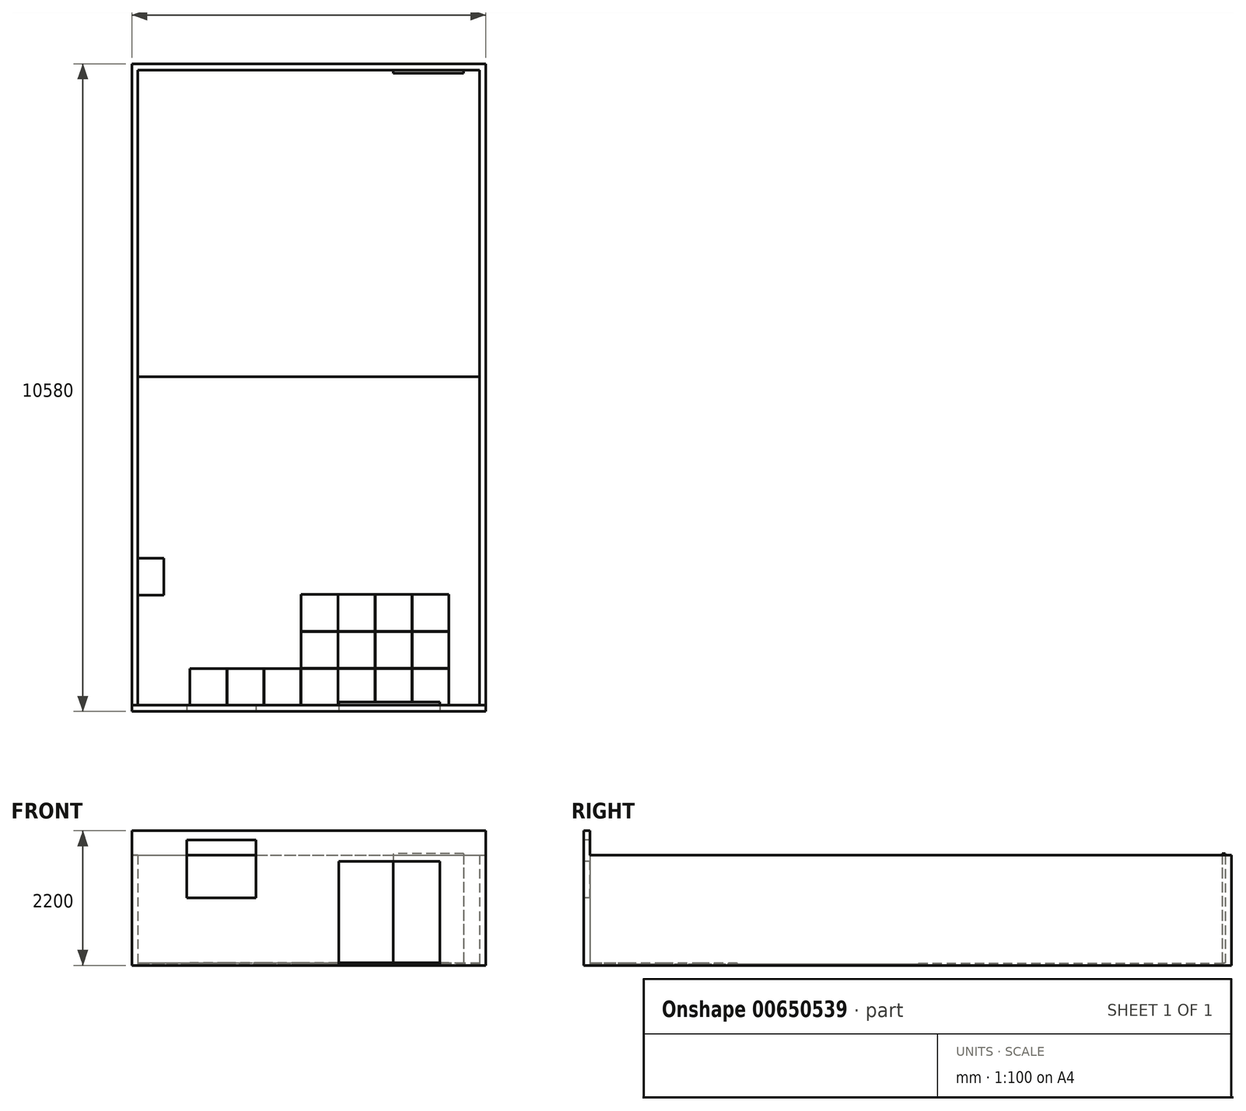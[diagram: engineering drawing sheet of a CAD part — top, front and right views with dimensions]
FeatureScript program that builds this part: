
annotation { "Feature Type Name" : "Feature", "Feature Type Description" : "" }
export const myFeature = defineFeature(function(context is Context, id is Id, definition is map)
    precondition{}
    {
        {
            var Q0;
            Q0=qCreatedBy(makeId("Top.planeOp"),FACE);
            var sketch = newSketch(context, id + "F0", { "sketchPlane" : qUnion([Q0])});
            skLineSegment(sketch, "E0.bottom", {"start": v(0, 0) * mm, "end": v(-5580, 0) * mm});
            skLineSegment(sketch, "E0.top", {"start": v(0, 10380) * mm, "end": v(-5580, 10380) * mm});
            skLineSegment(sketch, "E0.left", {"start": v(0, 0) * mm, "end": v(0, 10380) * mm});
            skLineSegment(sketch, "E0.right", {"start": v(-5580, 0) * mm, "end": v(-5580, 10380) * mm});
            skSolve(sketch);
        }
        {
            var Q0;
            Q0 = qSketchRegion(id + "F0", true);
            extrude(context, id + "F1", {"entities" : qUnion([Q0]), "depth" : 25 * mm, "offsetDistance" : 25 * mm});
        }
        {
            var Q0;
            Q0=makeQuery(id+"F1.opExtrude","CAP_FACE",FACE,{"disambiguationData":[OSD([sQuery(id+"F0.wireOp",EDGE,"E0.bottom"),sQuery(id+"F0.wireOp",EDGE,"E0.top"),sQuery(id+"F0.wireOp",EDGE,"E0.left"),sQuery(id+"F0.wireOp",EDGE,"E0.right")])],"isStart":false});
            var sketch = newSketch(context, id + "F2", { "sketchPlane" : qUnion([Q0])});
            skLineSegment(sketch, "E1.bottom", {"start": v(-500, 0) * mm, "end": v(-1100, 0) * mm});
            skLineSegment(sketch, "E1.top", {"start": v(-500, 600) * mm, "end": v(-1100, 600) * mm});
            skLineSegment(sketch, "E1.left", {"start": v(-500, 0) * mm, "end": v(-500, 600) * mm});
            skLineSegment(sketch, "E1.right", {"start": v(-1100, 0) * mm, "end": v(-1100, 600) * mm});
            skLineSegment(sketch, "E2.0.1.0", {"start": v(-500, 605) * mm, "end": v(-1100, 605) * mm});
            skLineSegment(sketch, "E2.0.1.1", {"start": v(-500, 1205) * mm, "end": v(-1100, 1205) * mm});
            skLineSegment(sketch, "E2.0.1.2", {"start": v(-500, 605) * mm, "end": v(-500, 1205) * mm});
            skLineSegment(sketch, "E2.0.1.3", {"start": v(-1100, 605) * mm, "end": v(-1100, 1205) * mm});
            skLineSegment(sketch, "E2.1.0.0", {"start": v(-1105, 0) * mm, "end": v(-1705, 0) * mm});
            skLineSegment(sketch, "E2.1.0.1", {"start": v(-1105, 600) * mm, "end": v(-1705, 600) * mm});
            skLineSegment(sketch, "E2.1.0.2", {"start": v(-1105, 0) * mm, "end": v(-1105, 600) * mm});
            skLineSegment(sketch, "E2.1.0.3", {"start": v(-1705, 0) * mm, "end": v(-1705, 600) * mm});
            skLineSegment(sketch, "E2.1.1.0", {"start": v(-1105, 605) * mm, "end": v(-1705, 605) * mm});
            skLineSegment(sketch, "E2.1.1.1", {"start": v(-1105, 1205) * mm, "end": v(-1705, 1205) * mm});
            skLineSegment(sketch, "E2.1.1.2", {"start": v(-1105, 605) * mm, "end": v(-1105, 1205) * mm});
            skLineSegment(sketch, "E2.1.1.3", {"start": v(-1705, 605) * mm, "end": v(-1705, 1205) * mm});
            skLineSegment(sketch, "E2.2.0.0", {"start": v(-1710, 0) * mm, "end": v(-2310, 0) * mm});
            skLineSegment(sketch, "E2.2.0.1", {"start": v(-1710, 600) * mm, "end": v(-2310, 600) * mm});
            skLineSegment(sketch, "E2.2.0.2", {"start": v(-1710, 0) * mm, "end": v(-1710, 600) * mm});
            skLineSegment(sketch, "E2.2.0.3", {"start": v(-2310, 0) * mm, "end": v(-2310, 600) * mm});
            skLineSegment(sketch, "E2.2.1.0", {"start": v(-1710, 605) * mm, "end": v(-2310, 605) * mm});
            skLineSegment(sketch, "E2.2.1.1", {"start": v(-1710, 1205) * mm, "end": v(-2310, 1205) * mm});
            skLineSegment(sketch, "E2.2.1.2", {"start": v(-1710, 605) * mm, "end": v(-1710, 1205) * mm});
            skLineSegment(sketch, "E2.2.1.3", {"start": v(-2310, 605) * mm, "end": v(-2310, 1205) * mm});
            skLineSegment(sketch, "E2.3.0.0", {"start": v(-2315, 0) * mm, "end": v(-2915, 0) * mm});
            skLineSegment(sketch, "E2.3.0.1", {"start": v(-2315, 600) * mm, "end": v(-2915, 600) * mm});
            skLineSegment(sketch, "E2.3.0.2", {"start": v(-2315, 0) * mm, "end": v(-2315, 600) * mm});
            skLineSegment(sketch, "E2.3.0.3", {"start": v(-2915, 0) * mm, "end": v(-2915, 600) * mm});
            skLineSegment(sketch, "E2.3.1.0", {"start": v(-2315, 605) * mm, "end": v(-2915, 605) * mm});
            skLineSegment(sketch, "E2.3.1.1", {"start": v(-2315, 1205) * mm, "end": v(-2915, 1205) * mm});
            skLineSegment(sketch, "E2.3.1.2", {"start": v(-2315, 605) * mm, "end": v(-2315, 1205) * mm});
            skLineSegment(sketch, "E2.3.1.3", {"start": v(-2915, 605) * mm, "end": v(-2915, 1205) * mm});
            skLineSegment(sketch, "E2.direction1", {"start": v(-1100, 0) * mm, "end": v(-1705, 0) * mm, "construction": true});
            skLineSegment(sketch, "E2.direction2", {"start": v(-1100, 0) * mm, "end": v(-1100, 605) * mm, "construction": true});
            skLineSegment(sketch, "E3.0.0.2", {"start": v(-500, 1210) * mm, "end": v(-1100, 1210) * mm});
            skLineSegment(sketch, "E3.3.0.2", {"start": v(-500, 1810) * mm, "end": v(-1100, 1810) * mm});
            skLineSegment(sketch, "E3.6.0.2", {"start": v(-500, 1210) * mm, "end": v(-500, 1810) * mm});
            skLineSegment(sketch, "E3.9.0.2", {"start": v(-1100, 1210) * mm, "end": v(-1100, 1810) * mm});
            skLineSegment(sketch, "E3.0.1.2", {"start": v(-1105, 1210) * mm, "end": v(-1705, 1210) * mm});
            skLineSegment(sketch, "E3.3.1.2", {"start": v(-1105, 1810) * mm, "end": v(-1705, 1810) * mm});
            skLineSegment(sketch, "E3.6.1.2", {"start": v(-1105, 1210) * mm, "end": v(-1105, 1810) * mm});
            skLineSegment(sketch, "E3.9.1.2", {"start": v(-1705, 1210) * mm, "end": v(-1705, 1810) * mm});
            skLineSegment(sketch, "E3.0.2.2", {"start": v(-1710, 1210) * mm, "end": v(-2310, 1210) * mm});
            skLineSegment(sketch, "E3.3.2.2", {"start": v(-1710, 1810) * mm, "end": v(-2310, 1810) * mm});
            skLineSegment(sketch, "E3.6.2.2", {"start": v(-1710, 1210) * mm, "end": v(-1710, 1810) * mm});
            skLineSegment(sketch, "E3.9.2.2", {"start": v(-2310, 1210) * mm, "end": v(-2310, 1810) * mm});
            skLineSegment(sketch, "E3.0.3.2", {"start": v(-2315, 1210) * mm, "end": v(-2915, 1210) * mm});
            skLineSegment(sketch, "E3.3.3.2", {"start": v(-2315, 1810) * mm, "end": v(-2915, 1810) * mm});
            skLineSegment(sketch, "E3.6.3.2", {"start": v(-2315, 1210) * mm, "end": v(-2315, 1810) * mm});
            skLineSegment(sketch, "E3.9.3.2", {"start": v(-2915, 1210) * mm, "end": v(-2915, 1810) * mm});
            skLineSegment(sketch, "E4.bottom", {"start": v(-500, 1815) * mm, "end": v(-1100, 1815) * mm});
            skLineSegment(sketch, "E5.direction1", {"start": v(-1100, 1810) * mm, "end": v(-1075, 1810) * mm, "construction": true});
            skLineSegment(sketch, "E6.bottom", {"start": v(-2920, 0) * mm, "end": v(-3520, 0) * mm});
            skLineSegment(sketch, "E6.top", {"start": v(-2920, 600) * mm, "end": v(-3520, 600) * mm});
            skLineSegment(sketch, "E6.left", {"start": v(-2920, 0) * mm, "end": v(-2920, 600) * mm});
            skLineSegment(sketch, "E6.right", {"start": v(-3520, 0) * mm, "end": v(-3520, 600) * mm});
            skLineSegment(sketch, "E7.1.0.0", {"start": v(-3525, 0) * mm, "end": v(-4125, 0) * mm});
            skLineSegment(sketch, "E7.1.0.1", {"start": v(-3525, 0) * mm, "end": v(-3525, 600) * mm});
            skLineSegment(sketch, "E7.1.0.2", {"start": v(-3525, 600) * mm, "end": v(-4125, 600) * mm});
            skLineSegment(sketch, "E7.1.0.3", {"start": v(-4125, 0) * mm, "end": v(-4125, 600) * mm});
            skLineSegment(sketch, "E7.2.0.0", {"start": v(-4130, 0) * mm, "end": v(-4730, 0) * mm});
            skLineSegment(sketch, "E7.2.0.1", {"start": v(-4130, 0) * mm, "end": v(-4130, 600) * mm});
            skLineSegment(sketch, "E7.2.0.2", {"start": v(-4130, 600) * mm, "end": v(-4730, 600) * mm});
            skLineSegment(sketch, "E7.2.0.3", {"start": v(-4730, 0) * mm, "end": v(-4730, 600) * mm});
            skLineSegment(sketch, "E7.2.0.4", {"start": v(-4125, 0) * mm, "end": v(-4125, 600) * mm});
            skLineSegment(sketch, "E7.direction1", {"start": v(-3520, 0) * mm, "end": v(-4125, 0) * mm, "construction": true});
            skSolve(sketch);
        }
        {
            var Q0;
            Q0 = qSketchRegion(id + "F2", true);
            var Q1;
            Q1=makeQuery(id+"F2.imprint","IMPRINT",FACE,{"disambiguationData":[TD([[makeQuery(id+"F2.imprint","IMPRINT",EDGE,{"derivedFrom":sQuery(id+"F2.wireOp",EDGE,"E2.2.1.0")}),-1.0]])]});
            var Q2;
            Q2=makeQuery(id+"F2.imprint","IMPRINT",FACE,{"disambiguationData":[TD([[makeQuery(id+"F2.imprint","IMPRINT",EDGE,{"derivedFrom":sQuery(id+"F2.wireOp",EDGE,"E2.1.1.0")}),-1.0]])]});
            extrude(context, id + "F3", {"entities" : qUnion([Q0, Q1, Q2]), "depth" : 15 * mm, "offsetDistance" : 25 * mm});
        }
        {
            var Q0;
            Q0=qCreatedBy(makeId("Top.planeOp"),FACE);
            var sketch = newSketch(context, id + "F4", { "sketchPlane" : qUnion([Q0])});
            skLineSegment(sketch, "E8.bottom", {"start": v(0, 0) * mm, "end": v(100, 0) * mm});
            skLineSegment(sketch, "E8.top", {"start": v(0, 10380) * mm, "end": v(100, 10380) * mm});
            skLineSegment(sketch, "E8.left", {"start": v(0, 0) * mm, "end": v(0, 10380) * mm});
            skLineSegment(sketch, "E8.right", {"start": v(100, 0) * mm, "end": v(100, 10380) * mm});
            skSolve(sketch);
        }
        {
            var Q0;
            Q0 = qSketchRegion(id + "F4", true);
            extrude(context, id + "F5", {"entities" : qUnion([Q0]), "operationType" : NewBodyOperationType.ADD, "depth" : 1800 * mm, "offsetDistance" : 25 * mm});
        }
        {
            var Q0;
            Q0=qCreatedBy(makeId("Top.planeOp"),FACE);
            var sketch = newSketch(context, id + "F6", { "sketchPlane" : qUnion([Q0])});
            skLineSegment(sketch, "E9.bottom", {"start": v(-5580, 10380) * mm, "end": v(100, 10380) * mm});
            skLineSegment(sketch, "E9.top", {"start": v(-5580, 10480) * mm, "end": v(100, 10480) * mm});
            skLineSegment(sketch, "E9.left", {"start": v(-5580, 10380) * mm, "end": v(-5580, 10480) * mm});
            skLineSegment(sketch, "E9.right", {"start": v(100, 10380) * mm, "end": v(100, 10480) * mm});
            skSolve(sketch);
        }
        {
            var Q0;
            Q0=makeQuery(id+"F6.imprint","IMPRINT",FACE,{"disambiguationData":[TD([[makeQuery(id+"F6.imprint","IMPRINT",EDGE,{"derivedFrom":sQuery(id+"F6.wireOp",EDGE,"E9.top")}),-1.0]])]});
            extrude(context, id + "F7", {"entities" : qUnion([Q0]), "operationType" : NewBodyOperationType.ADD, "depth" : 1800 * mm, "offsetDistance" : 25 * mm});
        }
        {
            var Q0;
            Q0=qCreatedBy(makeId("Top.planeOp"),FACE);
            var sketch = newSketch(context, id + "F8", { "sketchPlane" : qUnion([Q0])});
            skLineSegment(sketch, "E10.bottom", {"start": v(-5580, 0) * mm, "end": v(-5680, 0) * mm});
            skLineSegment(sketch, "E10.top", {"start": v(-5580, 10480) * mm, "end": v(-5680, 10480) * mm});
            skLineSegment(sketch, "E10.left", {"start": v(-5580, 0) * mm, "end": v(-5580, 10480) * mm});
            skLineSegment(sketch, "E10.right", {"start": v(-5680, 0) * mm, "end": v(-5680, 10480) * mm});
            skSolve(sketch);
        }
        {
            var Q0;
            Q0 = qSketchRegion(id + "F8", true);
            extrude(context, id + "F9", {"entities" : qUnion([Q0]), "operationType" : NewBodyOperationType.ADD, "depth" : 1800 * mm, "offsetDistance" : 25 * mm});
        }
        {
            var Q0;
            Q0=makeQuery(id+"F1.opExtrude","CAP_FACE",FACE,{"disambiguationData":[OSD([sQuery(id+"F0.wireOp",EDGE,"E0.bottom"),sQuery(id+"F0.wireOp",EDGE,"E0.top"),sQuery(id+"F0.wireOp",EDGE,"E0.left"),sQuery(id+"F0.wireOp",EDGE,"E0.right")])],"isStart":false});
            var sketch = newSketch(context, id + "F10", { "sketchPlane" : qUnion([Q0])});
            skLineSegment(sketch, "E11.bottom", {"start": v(-5580, 2400) * mm, "end": v(-5155, 2400) * mm});
            skLineSegment(sketch, "E11.top", {"start": v(-5580, 1800) * mm, "end": v(-5155, 1800) * mm});
            skLineSegment(sketch, "E11.left", {"start": v(-5580, 2400) * mm, "end": v(-5580, 1800) * mm});
            skLineSegment(sketch, "E11.right", {"start": v(-5155, 2400) * mm, "end": v(-5155, 1800) * mm});
            skSolve(sketch);
        }
        {
            var Q0;
            Q0 = qSketchRegion(id + "F10", true);
            extrude(context, id + "F11", {"entities" : qUnion([Q0]), "operationType" : NewBodyOperationType.ADD, "depth" : 15 * mm, "offsetDistance" : 25 * mm});
        }
        {
            var Q0;
            {var subQ6=sQuery(id+"F10.wireOp",EDGE,"E11.bottom");Q0=makeQuery(id+"F10.imprint","IMPRINT",FACE,{"disambiguationData":[TD([[makeQuery(id+"F10.imprint","IMPRINT",EDGE,{"derivedFrom":subQ6}),1.0]])]});}
            var sketch = newSketch(context, id + "F12", { "sketchPlane" : qUnion([Q0])});
            skLineSegment(sketch, "E12.bottom", {"start": v(-260, 10380) * mm, "end": v(-1410, 10380) * mm});
            skLineSegment(sketch, "E12.top", {"start": v(-260, 10330) * mm, "end": v(-1410, 10330) * mm});
            skLineSegment(sketch, "E12.left", {"start": v(-260, 10380) * mm, "end": v(-260, 10330) * mm});
            skLineSegment(sketch, "E12.right", {"start": v(-1410, 10380) * mm, "end": v(-1410, 10330) * mm});
            skSolve(sketch);
        }
        {
            var Q0;
            Q0 = qSketchRegion(id + "F12", true);
            extrude(context, id + "F13", {"entities" : qUnion([Q0]), "operationType" : NewBodyOperationType.ADD, "depth" : 1800 * mm, "offsetDistance" : 25 * mm});
        }
        {
            var Q0;
            Q0=qCreatedBy(makeId("Top.planeOp"),FACE);
            var sketch = newSketch(context, id + "F14", { "sketchPlane" : qUnion([Q0])});
            skLineSegment(sketch, "E13.bottom", {"start": v(-5680, 0) * mm, "end": v(100, 0) * mm});
            skLineSegment(sketch, "E13.top", {"start": v(-5680, -100) * mm, "end": v(100, -100) * mm});
            skLineSegment(sketch, "E13.left", {"start": v(-5680, 0) * mm, "end": v(-5680, -100) * mm});
            skLineSegment(sketch, "E13.right", {"start": v(100, 0) * mm, "end": v(100, -100) * mm});
            skSolve(sketch);
        }
        {
            var Q0;
            Q0 = qSketchRegion(id + "F14", true);
            extrude(context, id + "F15", {"entities" : qUnion([Q0]), "operationType" : NewBodyOperationType.ADD, "depth" : 2200 * mm, "offsetDistance" : 25 * mm});
        }
        {
            var Q0;
            Q0=makeQuery(id+"F15.opExtrude","SWEPT_FACE",FACE,{"disambiguationData":[OSD([sQuery(id+"F14.wireOp",EDGE,"E13.top")])]});
            var sketch = newSketch(context, id + "F16", { "sketchPlane" : qUnion([Q0])});
            skLineSegment(sketch, "E14.bottom", {"start": v(-650, 0) * mm, "end": v(-2300, 0) * mm});
            skLineSegment(sketch, "E14.top", {"start": v(-650, 1700) * mm, "end": v(-2300, 1700) * mm});
            skLineSegment(sketch, "E14.left", {"start": v(-650, 0) * mm, "end": v(-650, 1700) * mm});
            skLineSegment(sketch, "E14.right", {"start": v(-2300, 0) * mm, "end": v(-2300, 1700) * mm});
            skLineSegment(sketch, "E15.bottom", {"start": v(-4780, 2050) * mm, "end": v(-3650, 2050) * mm});
            skLineSegment(sketch, "E15.top", {"start": v(-4780, 1100) * mm, "end": v(-3650, 1100) * mm});
            skLineSegment(sketch, "E15.left", {"start": v(-4780, 2050) * mm, "end": v(-4780, 1100) * mm});
            skLineSegment(sketch, "E15.right", {"start": v(-3650, 2050) * mm, "end": v(-3650, 1100) * mm});
            skSolve(sketch);
        }
        {
            var Q0;
            Q0 = qSketchRegion(id + "F16", true);
            extrude(context, id + "F17", {"entities" : qUnion([Q0]), "operationType" : NewBodyOperationType.REMOVE, "flatOperationType" : FlatOperationType.REMOVE, "thickness1" : 5 * mm, "thickness2" : 0 * mm, "thickness" : 5 * mm, "oppositeDirection" : true, "depth" : 150 * mm, "offsetDistance" : 25 * mm, "startOffsetBound" : StartOffsetType.BLIND, "startOffsetDistance" : 25 * mm, "domain" : OperationDomain.MODEL});
        }
        {
            var Q0;
            Q0=makeQuery(id+"F1.opExtrude","CAP_FACE",FACE,{"disambiguationData":[OSD([sQuery(id+"F0.wireOp",EDGE,"E0.bottom"),sQuery(id+"F0.wireOp",EDGE,"E0.top"),sQuery(id+"F0.wireOp",EDGE,"E0.left"),sQuery(id+"F0.wireOp",EDGE,"E0.right")])],"isStart":false});
            var sketch = newSketch(context, id + "F18", { "sketchPlane" : qUnion([Q0]), "disableImprinting" : false});
            skLineSegment(sketch, "E16.top", {"start": v(0, 5369.96) * mm, "end": v(-5580, 5369.96) * mm});
            skLineSegment(sketch, "E16.left", {"start": v(0, 9430) * mm, "end": v(0, 5369.96) * mm});
            skLineSegment(sketch, "E16.right", {"start": v(-5580, 9430) * mm, "end": v(-5580, 5369.96) * mm});
            skLineSegment(sketch, "E17.top", {"start": v(0, 10380) * mm, "end": v(-5580, 10380) * mm});
            skLineSegment(sketch, "E17.left", {"start": v(0, 9430) * mm, "end": v(0, 10380) * mm});
            skLineSegment(sketch, "E17.right", {"start": v(-5580, 9430) * mm, "end": v(-5580, 10380) * mm});
            skSolve(sketch);
        }
        {
            var Q0;
            Q0 = qSketchRegion(id + "F18", true);
            extrude(context, id + "F19", {"entities" : qUnion([Q0]), "operationType" : NewBodyOperationType.ADD, "depth" : 10 * mm, "offsetDistance" : 25 * mm});
        }
    });
